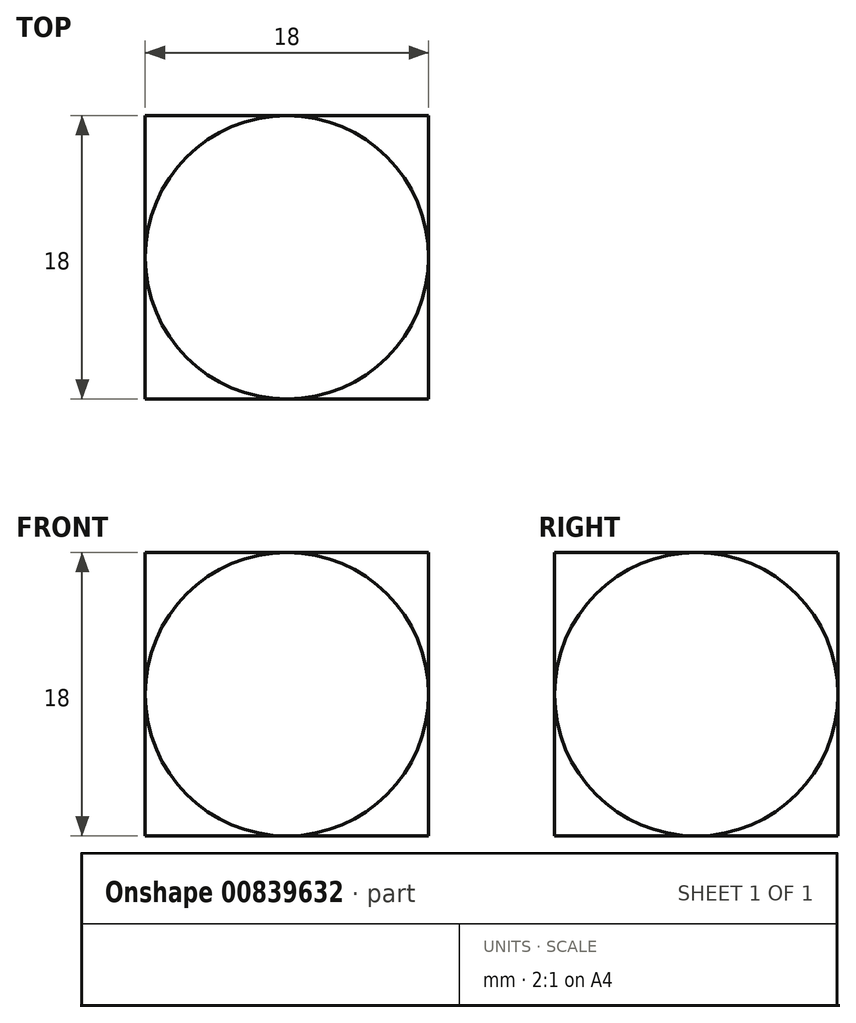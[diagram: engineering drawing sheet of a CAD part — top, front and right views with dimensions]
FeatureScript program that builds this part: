
annotation { "Feature Type Name" : "Feature", "Feature Type Description" : "" }
export const myFeature = defineFeature(function(context is Context, id is Id, definition is map)
    precondition{}
    {
        {
            var Q0;
            Q0=qCreatedBy(makeId("Front.planeOp"),FACE);
            var sketch = newSketch(context, id + "F0", { "sketchPlane" : qUnion([Q0])});
            skLineSegment(sketch, "E0.bottom", {"start": v(9, -9) * mm, "end": v(-9, -9) * mm});
            skLineSegment(sketch, "E0.top", {"start": v(9, 9) * mm, "end": v(-9, 9) * mm});
            skLineSegment(sketch, "E0.left", {"start": v(9, -9) * mm, "end": v(9, 9) * mm});
            skLineSegment(sketch, "E0.right", {"start": v(-9, -9) * mm, "end": v(-9, 9) * mm});
            skPoint(sketch, "E0.middle", {"position": v(0, 0) * mm});
            skSolve(sketch);
        }
        {
            var Q0;
            Q0 = qSketchRegion(id + "F0", true);
            extrude(context, id + "F1", {"entities" : qUnion([Q0]), "endBound" : BoundingType.SYMMETRIC, "depth" : 18 * mm, "offsetDistance" : 25 * mm});
        }
        {
            var Q0;
            Q0=qCreatedBy(makeId("Front.planeOp"),FACE);
            var sketch = newSketch(context, id + "F2", { "sketchPlane" : qUnion([Q0])});
            skCircle(sketch, "E1", {"center": v(0, 0) * mm, "radius": 12.73 * mm});
            skLineSegment(sketch, "E2", {"start": v(-14.28, 0) * mm, "end": v(14.9, 0) * mm});
            skSolve(sketch);
        }
        {
            var Q0;
            {var subQ0=sQuery(id+"F2.wireOp",EDGE,"E2");var subQ1=sQuery(id+"F2.wireOp",EDGE,"E1");var subQ2=makeQuery(id+"F2.imprint","INTERSECT",VERTEX,{"disambiguationData":[OD(0.0)],"derivedFrom":[subQ1,subQ0]});Q0=makeQuery(id+"F2.imprint","IMPRINT",FACE,{"disambiguationData":[TD([[makeQuery(id+"F2.imprint","IMPRINT",EDGE,{"disambiguationData":[TD([[subQ2,-1.0]])],"derivedFrom":subQ1}),1.0]])]});}
            var Q1;
            Q1=sQuery(id+"F2.wireOp",EDGE,"E2");
            revolve(context, id + "F3", {"surfaceOperationType" : NewSurfaceOperationType.NEW, "entities" : qUnion([Q0]), "axis" : qUnion([Q1]), "revolveType" : RevolveType.FULL});
        }
        {
            var Q0;
            Q0=makeQuery(id+"F1.opExtrude","SWEPT_BODY",BODY,{"disambiguationData":[OSD([sQuery(id+"F0.wireOp",EDGE,"E0.bottom"),sQuery(id+"F0.wireOp",EDGE,"E0.top"),sQuery(id+"F0.wireOp",EDGE,"E0.left"),sQuery(id+"F0.wireOp",EDGE,"E0.right")])]});
            var Q1;
            Q1=makeQuery(id+"F3.opRevolve","SWEPT_BODY",BODY,{"disambiguationData":[OSD([sQuery(id+"F2.wireOp",EDGE,"E1"),sQuery(id+"F2.wireOp",EDGE,"E2")])]});
            booleanBodies(context, id + "F4", {"operationType" : BooleanOperationType.INTERSECTION, "tools" : qUnion([Q0, Q1])});
        }
    });
